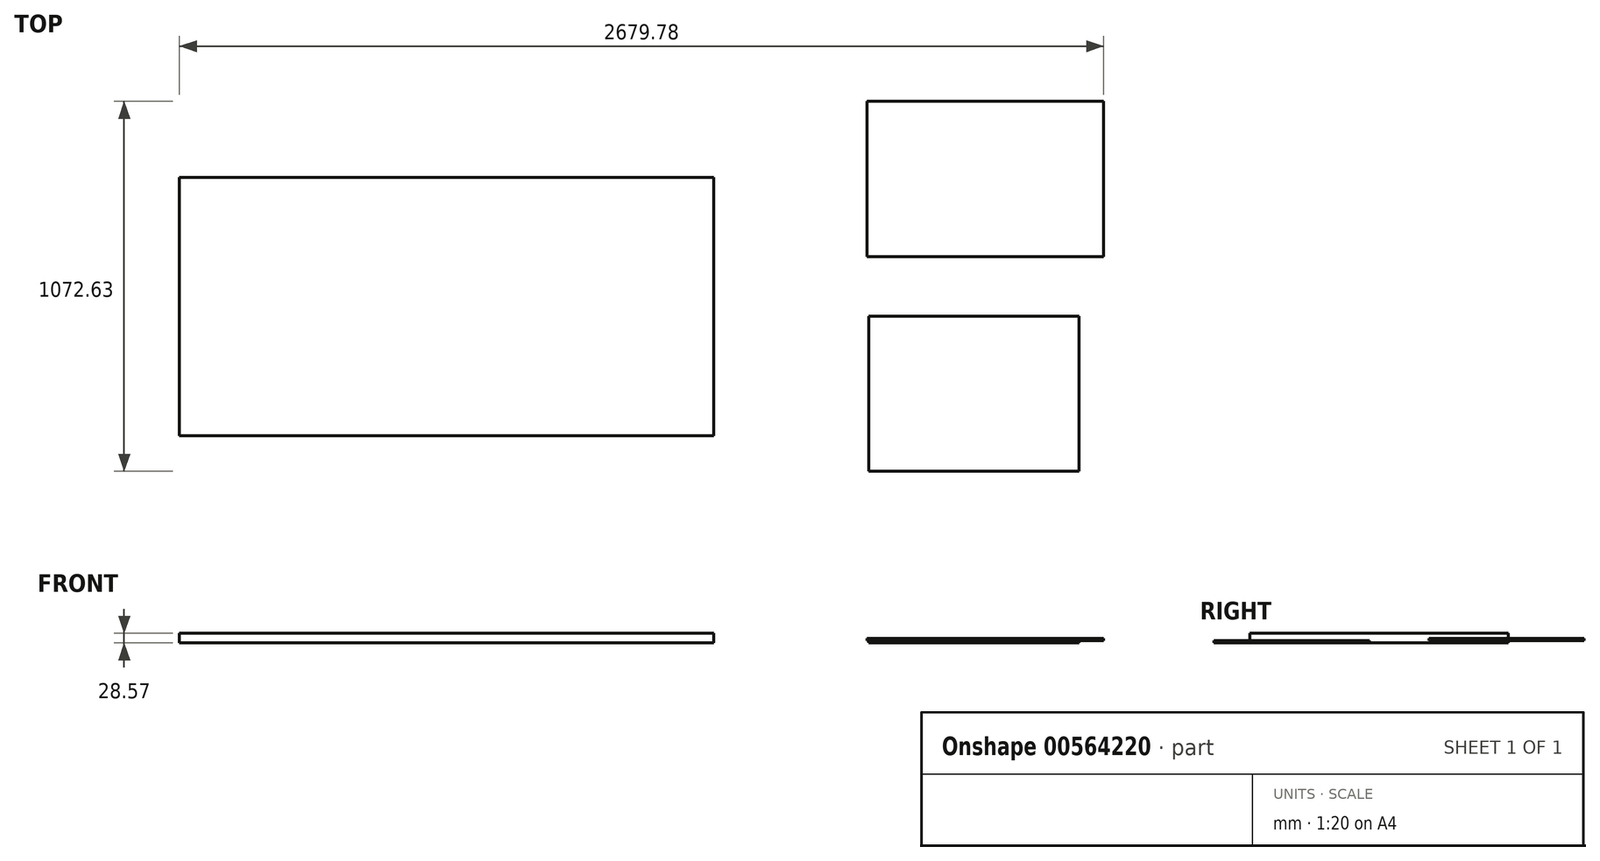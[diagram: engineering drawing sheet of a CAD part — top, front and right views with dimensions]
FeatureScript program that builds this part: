
annotation { "Feature Type Name" : "Feature", "Feature Type Description" : "" }
export const myFeature = defineFeature(function(context is Context, id is Id, definition is map)
    precondition{}
    {
        {
            var Q0;
            Q0=qCreatedBy(makeId("Top.planeOp"),FACE);
            var sketch = newSketch(context, id + "F0", { "sketchPlane" : qUnion([Q0])});
            skLineSegment(sketch, "E0.bottom", {"start": v(-2407.4, 710.4) * mm, "end": v(-858, 710.4) * mm});
            skLineSegment(sketch, "E0.top", {"start": v(-2407.4, -38.9) * mm, "end": v(-858, -38.9) * mm});
            skLineSegment(sketch, "E0.left", {"start": v(-2407.4, 710.4) * mm, "end": v(-2407.4, -38.9) * mm});
            skLineSegment(sketch, "E0.right", {"start": v(-858, 710.4) * mm, "end": v(-858, -38.9) * mm});
            skSolve(sketch);
        }
        {
            var Q0;
            Q0=makeQuery(id+"F0.imprint","IMPRINT",FACE,{"disambiguationData":[TD([[makeQuery(id+"F0.imprint","IMPRINT",EDGE,{"derivedFrom":sQuery(id+"F0.wireOp",EDGE,"E0.bottom")}),-1.0]])]});
            extrude(context, id + "F1", {"entities" : qUnion([Q0]), "depth" : 28.57 * mm, "offsetDistance" : 25.4 * mm});
        }
        {
            var Q0;
            Q0=qCreatedBy(makeId("Top.planeOp"),FACE);
            var sketch = newSketch(context, id + "F2", { "sketchPlane" : qUnion([Q0])});
            skLineSegment(sketch, "E1.bottom", {"start": v(-408.83, 307.88) * mm, "end": v(200.77, 307.88) * mm});
            skLineSegment(sketch, "E1.top", {"start": v(-408.83, -142.2) * mm, "end": v(200.77, -142.2) * mm});
            skLineSegment(sketch, "E1.left", {"start": v(-408.83, 307.88) * mm, "end": v(-408.83, -142.2) * mm});
            skLineSegment(sketch, "E1.right", {"start": v(200.77, 307.88) * mm, "end": v(200.77, -142.2) * mm});
            skSolve(sketch);
        }
        {
            var Q0;
            Q0=makeQuery(id+"F2.imprint","IMPRINT",FACE,{"disambiguationData":[TD([[makeQuery(id+"F2.imprint","IMPRINT",EDGE,{"derivedFrom":sQuery(id+"F2.wireOp",EDGE,"E1.bottom")}),-1.0]])]});
            extrude(context, id + "F3", {"entities" : qUnion([Q0]), "depth" : 6.35 * mm, "offsetDistance" : 25.4 * mm});
        }
        {
            var Q0;
            Q0=makeQuery(id+"F3.opExtrude","CAP_FACE",FACE,{"disambiguationData":[OSD([sQuery(id+"F2.wireOp",EDGE,"E1.bottom"),sQuery(id+"F2.wireOp",EDGE,"E1.top"),sQuery(id+"F2.wireOp",EDGE,"E1.left"),sQuery(id+"F2.wireOp",EDGE,"E1.right")])],"isStart":false});
            var sketch = newSketch(context, id + "F4", { "sketchPlane" : qUnion([Q0])});
            skLineSegment(sketch, "E2.bottom", {"start": v(-413.4, 930.43) * mm, "end": v(272.4, 930.43) * mm});
            skLineSegment(sketch, "E2.top", {"start": v(-413.4, 480.34) * mm, "end": v(272.4, 480.34) * mm});
            skLineSegment(sketch, "E2.left", {"start": v(-413.4, 930.43) * mm, "end": v(-413.4, 480.34) * mm});
            skLineSegment(sketch, "E2.right", {"start": v(272.4, 930.43) * mm, "end": v(272.4, 480.34) * mm});
            skSolve(sketch);
        }
        {
            var Q0;
            Q0=makeQuery(id+"F4.imprint","IMPRINT",FACE,{"disambiguationData":[TD([[makeQuery(id+"F4.imprint","IMPRINT",EDGE,{"derivedFrom":sQuery(id+"F4.wireOp",EDGE,"E2.bottom")}),-1.0]])]});
            extrude(context, id + "F5", {"entities" : qUnion([Q0]), "depth" : 6.35 * mm, "offsetDistance" : 25.4 * mm});
        }
    });
